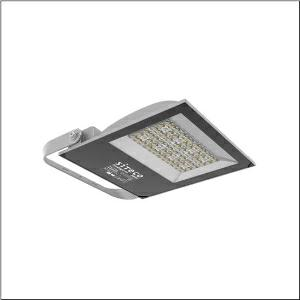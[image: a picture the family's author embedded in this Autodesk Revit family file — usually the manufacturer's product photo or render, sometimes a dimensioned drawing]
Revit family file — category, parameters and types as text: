
# Revit family: floodlight_fl_41_midi___pl32_5xa8581b2121_e0cb
name_source: partatom
category: Lighting Fixtures
units: mm (PartAtom-declared; Revit-internal decimal feet)

## family parameters
Cut with Voids When Loaded = No
Host = Face
Light Source = No
Part Type = Normal
Room Calculation Point = No
Round Connector Dimension = Use Diameter
Shared = No

## types (1)
- --- (1 x LED, 26000 lm, 200 W, 4000K)
    Apparent Load = 200 VA
    CIE Flux Codes = 38 75 98 100 100
    Color Rendering = 70
    Color Temperature = 4000K
    Default Elevation = 1800 mm
    Description = Floodlight FL 41 midi, floodlight, primary light control with lens, of PMMA, primary optical cover: protective disc, transparent, light distribution: PL32, light emission: direct distribution, installation type: surface-mounted, LED, High Power LED, rated luminous flux: 26.000lm, luminous efficacy: 130lm/W, light colour: 740, colour temperature: 4000K, control gear: ON/OFF Multilumen, with cable, 3x 1.5mm², mains connection: 220..240V, AC, 50/60Hz, connection cable pre-assembled, cable length: 2m, rated input power: 200W, luminaire housing, of diecast aluminium, powder-coated, metallic grey (RAL 9006), length: 375mm, width: 335mm, height: 65mm, protection rating (complete): IP65, insulation class (complete): insulation class I (protective earthing), certification: CE, ENEC, impact resistance: IK08, permissible operating ambient temperature: -40..+40°C, permissible storage temperature: -40..+60°C, packaging unit: 1 piece

Light Distribution: PL32
    Height = 66 mm
    Lamp = 1 x LED
    Lamp Light Flux = 26000 lm
    Lamp Power = 200 W
    Lamp count = 1
    Length = 323 mm
    Luminous efficacy = 130 lm/W
    Manufacturer = Siteco
    ModVariant = No
    Model = 5XA8581B2121
    Mounting Place = Ceiling
    Mounting Type = Surface mounted
    Number of Poles = 1
    OnlyDefault = Yes
    Power Factor = 1
    Product Name = Floodlight FL 41 midi | PL32
    Product group = floodlight | ceiling mounted
    ProductGroupID = 305
    Protection Class = Protection class I
    Protection Degree = IP 65
    RLX_Detail_Level = 1
    RLX_Emergency_Light_Flux = 0 lm
    RLX_Emergency_Type = 0
    RLX_Emergency_Type_DB = No
    RlxData = <blob elided: 27417 chars, md5=2447ae4e>
    Socket = socket
    Standby Power = 0 W
    System Light Flux = 26000 lm
    System Power = 200 W
    Type Comments = factory setting: luminous flux: 100 % | (OFF | OFF | OFF)
    Type Image = l_1248229.jpg
    URL = http://relux.com
    VarID = @adj_132749
    Voltage = 0 V
    Weight = 0.00 kg
    Width = 331 mm

## geometry (parser evidence)
native form markers: Blend x4, Sweep x10
no freeform markers — native parametric forms only
